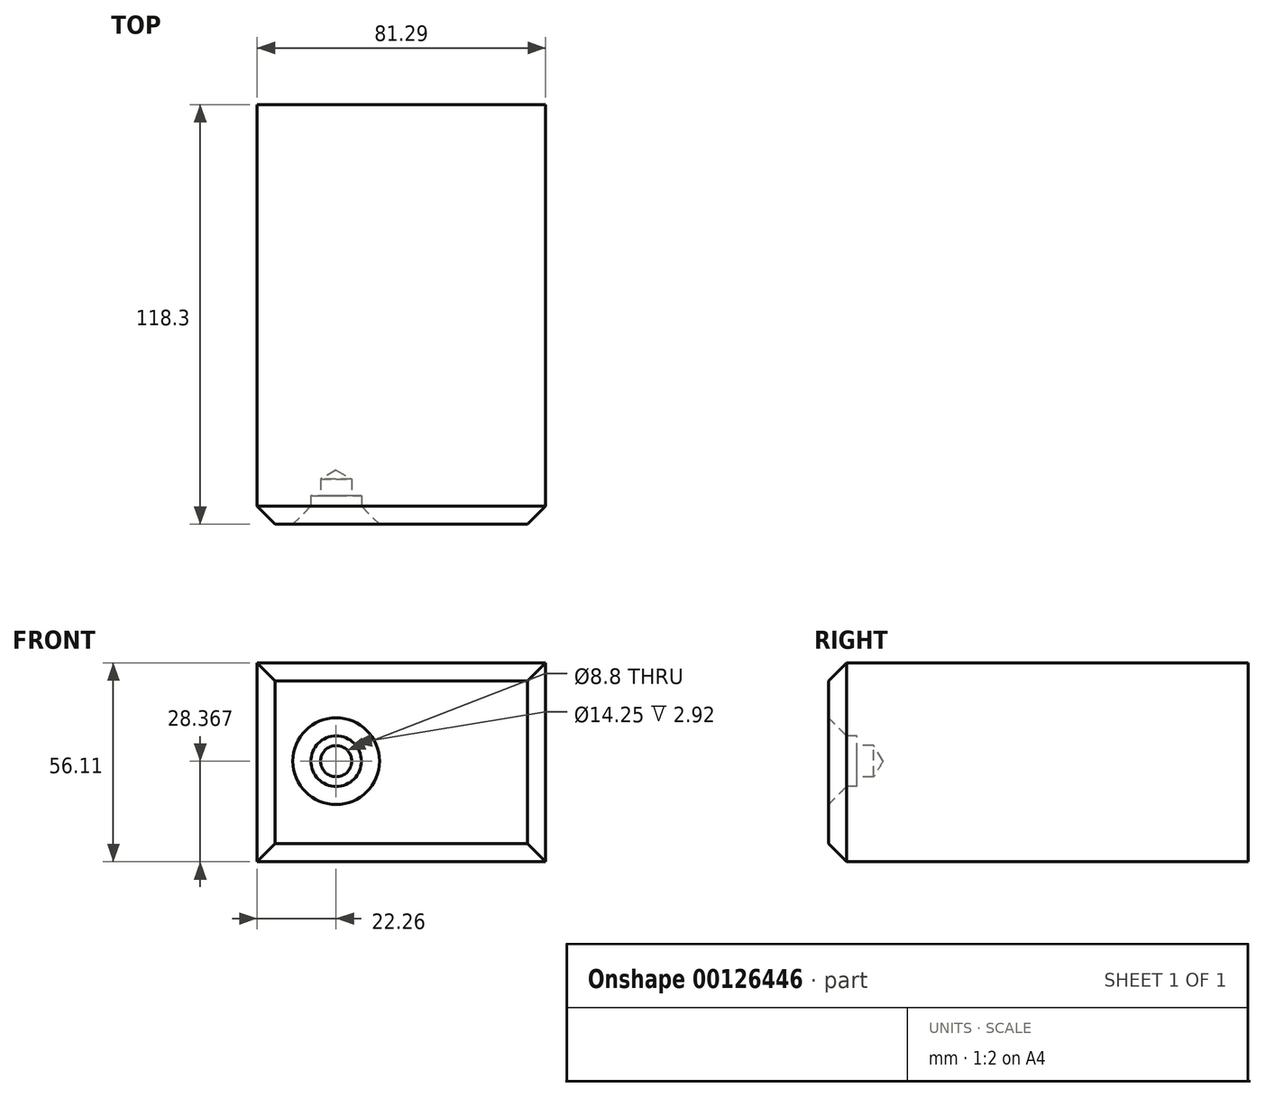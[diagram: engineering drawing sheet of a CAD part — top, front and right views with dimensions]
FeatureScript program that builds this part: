
annotation { "Feature Type Name" : "Feature", "Feature Type Description" : "" }
export const myFeature = defineFeature(function(context is Context, id is Id, definition is map)
    precondition{}
    {
        {
            var Q0;
            Q0=qCreatedBy(makeId("Front.planeOp"),FACE);
            var sketch = newSketch(context, id + "F0", { "sketchPlane" : qUnion([Q0])});
            skLineSegment(sketch, "E0.bottom", {"start": v(-28.24, 4.9) * mm, "end": v(53.05, 4.9) * mm});
            skLineSegment(sketch, "E0.top", {"start": v(-28.24, -51.21) * mm, "end": v(53.05, -51.21) * mm});
            skLineSegment(sketch, "E0.left", {"start": v(-28.24, 4.9) * mm, "end": v(-28.24, -51.21) * mm});
            skLineSegment(sketch, "E0.right", {"start": v(53.05, 4.9) * mm, "end": v(53.05, -51.21) * mm});
            skSolve(sketch);
        }
        {
            var Q0;
            Q0=makeQuery(id+"F0.imprint","IMPRINT",FACE,{"disambiguationData":[TD([[makeQuery(id+"F0.imprint","IMPRINT",EDGE,{"derivedFrom":sQuery(id+"F0.wireOp",EDGE,"E0.bottom")}),-1.0]])]});
            extrude(context, id + "F1", {"entities" : qUnion([Q0]), "depth" : 118.3 * mm});
        }
        {
            var Q0;
            Q0=makeQuery(id+"F1.opExtrude","CAP_FACE",FACE,{"disambiguationData":[OSD([sQuery(id+"F0.wireOp",EDGE,"E0.bottom"),sQuery(id+"F0.wireOp",EDGE,"E0.top"),sQuery(id+"F0.wireOp",EDGE,"E0.left"),sQuery(id+"F0.wireOp",EDGE,"E0.right")])],"isStart":false});
            var sketch = newSketch(context, id + "F2", { "sketchPlane" : qUnion([Q0])});
            skPoint(sketch, "E1", {"position": v(-5.98, -22.84) * mm});
            skSolve(sketch);
        }
        {
            var Q0;
            Q0=sQuery(id+"F2.wireOp",VERTEX,"E1");
            var Q1;
            Q1=makeQuery(id+"F1.opExtrude","SWEPT_BODY",BODY,{"disambiguationData":[OSD([sQuery(id+"F0.wireOp",EDGE,"E0.bottom"),sQuery(id+"F0.wireOp",EDGE,"E0.top"),sQuery(id+"F0.wireOp",EDGE,"E0.left"),sQuery(id+"F0.wireOp",EDGE,"E0.right")])]});
            hole(context, id + "F3", {"style" : HoleStyle.C_BORE, "endStyle" : HoleEndStyle.BLIND, "standardTappedOrClearance" : lookupTablePath({ "standard" : "ISO", "fit" : "Normal", "size" : "M8", "type" : "Clearance" }), "standardBlindInLast" : lookupTablePath({ "fit" : "Standard", "standard" : "ISO", "size" : "M8", "type" : "Clearance" }), "holeDiameter" : 8.8 * mm, "cBoreDiameter" : 14.25 * mm, "cBoreDepth" : 8 * mm, "holeDepth" : 12.7 * mm, "locations" : qUnion([Q0]), "scope" : qUnion([Q1])});
        }
        {
            var Q0;
            Q0=makeQuery(id+"F1.opExtrude","CAP_FACE",FACE,{"disambiguationData":[OSD([sQuery(id+"F0.wireOp",EDGE,"E0.bottom"),sQuery(id+"F0.wireOp",EDGE,"E0.top"),sQuery(id+"F0.wireOp",EDGE,"E0.left"),sQuery(id+"F0.wireOp",EDGE,"E0.right")])],"isStart":false});
            chamfer(context, id + "F4", {"entities" : qUnion([Q0]), "width" : 5.08 * mm, "tangentPropagation" : true});
        }
    });
